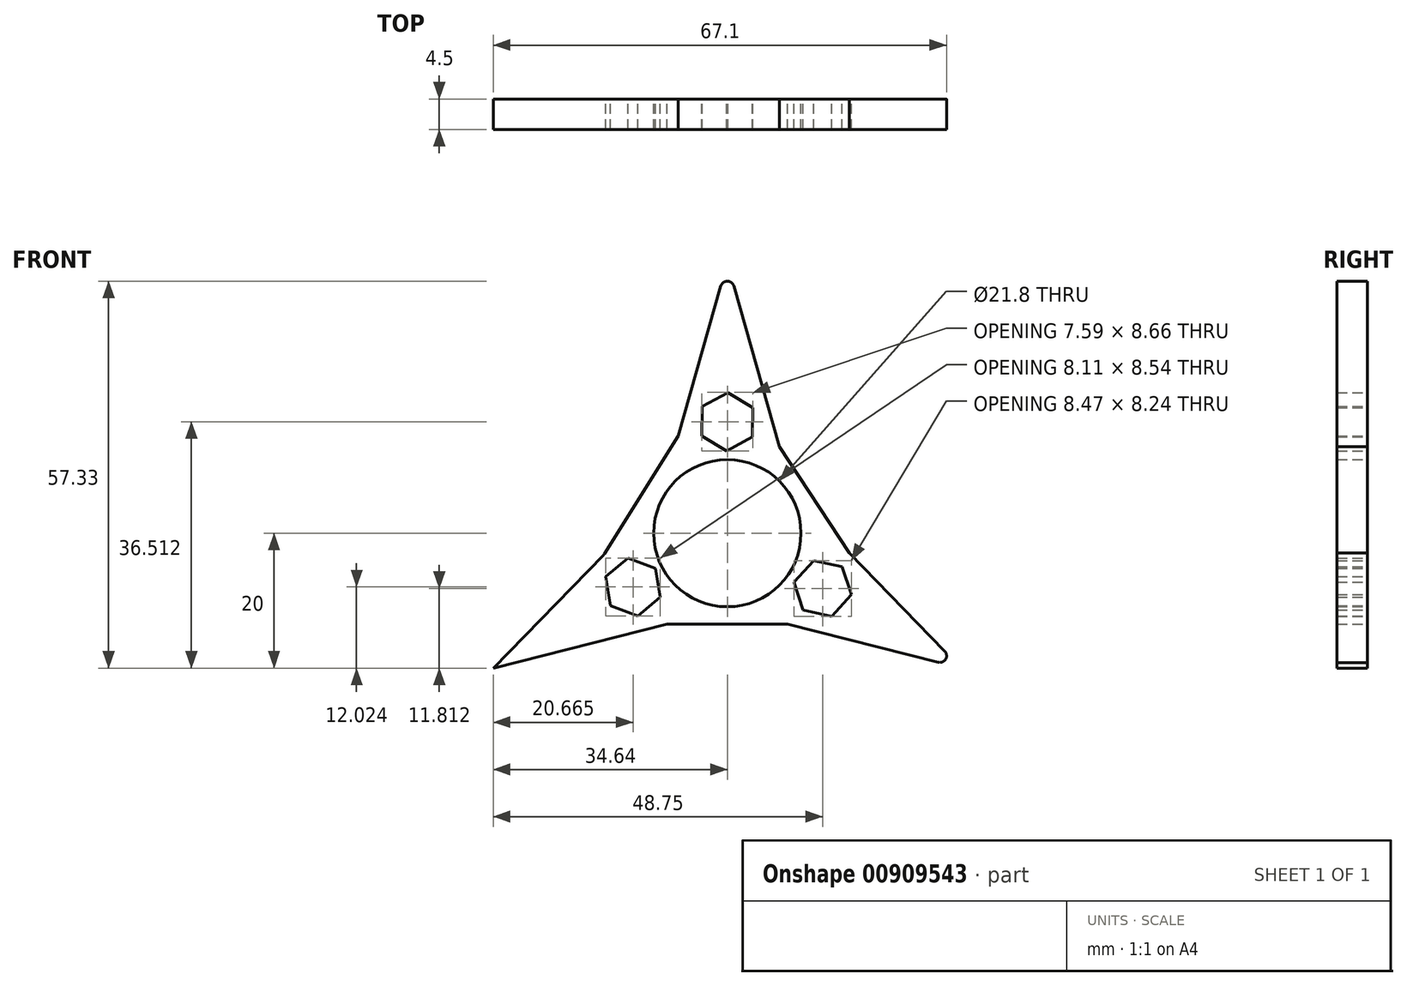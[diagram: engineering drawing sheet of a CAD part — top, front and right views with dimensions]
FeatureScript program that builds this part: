
annotation { "Feature Type Name" : "Feature", "Feature Type Description" : "" }
export const myFeature = defineFeature(function(context is Context, id is Id, definition is map)
    precondition{}
    {
        {
            var Q0;
            Q0=qCreatedBy(makeId("Front.planeOp"),FACE);
            var sketch = newSketch(context, id + "F0", { "sketchPlane" : qUnion([Q0])});
            skCircle(sketch, "E0", {"center": v(0, 0) * mm, "radius": 10.9 * mm});
            skLineSegment(sketch, "E1", {"start": v(0, 0) * mm, "end": v(0, 40) * mm});
            skLineSegment(sketch, "E2", {"start": v(0, 0) * mm, "end": v(34.64, -20) * mm});
            skPoint(sketch, "E3.MirrorCS.start.orphan", {"position": v(0, 40) * mm});
            skLineSegment(sketch, "E4", {"start": v(0, 40) * mm, "end": v(7.7, 12.82) * mm});
            skLineSegment(sketch, "E5", {"start": v(0, 0) * mm, "end": v(-34.64, -20) * mm});
            skPoint(sketch, "E6.MirrorP", {"position": v(-34.64, -20) * mm});
            skLineSegment(sketch, "E7.MirrorCS", {"start": v(-34.64, -20) * mm, "end": v(-18.27, -3.15) * mm});
            skLineSegment(sketch, "E8.MirrorCS", {"start": v(-34.64, -20) * mm, "end": v(-8.93, -13.5) * mm});
            skLineSegment(sketch, "E9.MirrorCS", {"start": v(0, 40) * mm, "end": v(-7.26, 14.37) * mm});
            skLineSegment(sketch, "E10.MirrorCS", {"start": v(34.64, -20) * mm, "end": v(18.08, -2.97) * mm});
            skLineSegment(sketch, "E11.MirrorCS", {"start": v(34.64, -20) * mm, "end": v(8.93, -13.5) * mm});
            skLineSegment(sketch, "E12", {"start": v(7.7, 12.82) * mm, "end": v(18.08, -2.97) * mm});
            skLineSegment(sketch, "E13", {"start": v(-7.26, 14.37) * mm, "end": v(-18.27, -3.15) * mm});
            skLineSegment(sketch, "E14", {"start": v(8.93, -13.5) * mm, "end": v(-8.93, -13.5) * mm});
            skPoint(sketch, "E15.orphan", {"position": v(15.2, 0) * mm});
            skPoint(sketch, "E16.end.orphan", {"position": v(-15.2, 0) * mm});
            skSolve(sketch);
        }
        {
            var Q0;
            Q0=qSketchRegion(id+"F0",true);
            extrude(context, id + "F1", {"entities" : qUnion([Q0]), "depth" : 4.5 * mm, "offsetDistance" : 25 * mm});
        }
        {
            var Q0;
            Q0=makeQuery(id+"F1.opExtrude","SWEPT_EDGE",EDGE,{"disambiguationData":[OSD([sQuery(id+"F0.wireOp",EDGE,"E1"),sQuery(id+"F0.wireOp",EDGE,"E4"),sQuery(id+"F0.wireOp",EDGE,"E9.MirrorCS")])]});
            var Q1;
            Q1=makeQuery(id+"F1.opExtrude","SWEPT_EDGE",EDGE,{"disambiguationData":[OSD([sQuery(id+"F0.wireOp",EDGE,"E2"),sQuery(id+"F0.wireOp",EDGE,"E10.MirrorCS"),sQuery(id+"F0.wireOp",EDGE,"E11.MirrorCS")])]});
            var Q2;
            Q2=makeQuery(id+"F1.opExtrude","SWEPT_EDGE",EDGE,{"disambiguationData":[OSD([sQuery(id+"F0.wireOp",EDGE,"E7.MirrorCS"),sQuery(id+"F0.wireOp",EDGE,"E5"),sQuery(id+"F0.wireOp",EDGE,"E8.MirrorCS")])]});
            fillet(context, id + "F2", {"entities" : qUnion([Q0, Q1, Q2]), "radius" : 1 * mm, "tangentPropagation" : true, "allowEdgeOverflow" : false});
        }
        {
            var Q0;
            Q0=makeQuery(id+"F1.opExtrude","CAP_FACE",FACE,{"disambiguationData":[OSD([sQuery(id+"F0.wireOp",EDGE,"E0"),sQuery(id+"F0.wireOp",EDGE,"E4"),sQuery(id+"F0.wireOp",EDGE,"E7.MirrorCS"),sQuery(id+"F0.wireOp",EDGE,"E9.MirrorCS"),sQuery(id+"F0.wireOp",EDGE,"E8.MirrorCS"),sQuery(id+"F0.wireOp",EDGE,"E10.MirrorCS"),sQuery(id+"F0.wireOp",EDGE,"E11.MirrorCS"),sQuery(id+"F0.wireOp",EDGE,"E16"),sQuery(id+"F0.wireOp",EDGE,"dIhDfe71-4vUS-nJFN-CgB5-YhKECHlm1RoW"),sQuery(id+"F0.wireOp",EDGE,"exgupVJA-VvQW-esT0-tabG-CJ82kmzNKVRX")])],"isStart":true});
            var sketch = newSketch(context, id + "F3", { "sketchPlane" : qUnion([Q0])});
            skCircle(sketch, "E17.cCircle", {"center": v(-14.11, -8.19) * mm, "radius": 3.75 * mm, "construction": true});
            skLineSegment(sketch, "E17.0", {"start": v(-9.88, -7.29) * mm, "end": v(-11.21, -11.4) * mm});
            skLineSegment(sketch, "E17.1", {"start": v(-11.21, -11.4) * mm, "end": v(-15.45, -12.3) * mm});
            skLineSegment(sketch, "E17.2", {"start": v(-15.45, -12.3) * mm, "end": v(-18.35, -9.1) * mm});
            skLineSegment(sketch, "E17.3", {"start": v(-18.35, -9.1) * mm, "end": v(-17, -4.97) * mm});
            skLineSegment(sketch, "E17.4", {"start": v(-17, -4.97) * mm, "end": v(-12.77, -4.07) * mm});
            skLineSegment(sketch, "E17.5", {"start": v(-12.77, -4.07) * mm, "end": v(-9.88, -7.29) * mm});
            skPoint(sketch, "E17.0.midPoint", {"position": v(-10.54, -9.34) * mm});
            skCircle(sketch, "E18.cCircle", {"center": v(13.97, -7.98) * mm, "radius": 3.75 * mm, "construction": true});
            skLineSegment(sketch, "E18.0", {"start": v(18.03, -6.45) * mm, "end": v(17.32, -10.72) * mm});
            skLineSegment(sketch, "E18.1", {"start": v(17.32, -10.72) * mm, "end": v(13.27, -12.25) * mm});
            skLineSegment(sketch, "E18.2", {"start": v(13.27, -12.25) * mm, "end": v(9.92, -9.5) * mm});
            skLineSegment(sketch, "E18.3", {"start": v(9.92, -9.5) * mm, "end": v(10.63, -5.23) * mm});
            skLineSegment(sketch, "E18.4", {"start": v(10.63, -5.23) * mm, "end": v(14.68, -3.7) * mm});
            skLineSegment(sketch, "E18.5", {"start": v(14.68, -3.7) * mm, "end": v(18.03, -6.45) * mm});
            skPoint(sketch, "E18.0.midPoint", {"position": v(17.67, -8.59) * mm});
            skCircle(sketch, "E19.cCircle", {"center": v(0, 16.51) * mm, "radius": 3.75 * mm, "construction": true});
            skLineSegment(sketch, "E19.0", {"start": v(3.8, 14.43) * mm, "end": v(0.1, 12.18) * mm});
            skLineSegment(sketch, "E19.1", {"start": v(0.1, 12.18) * mm, "end": v(-3.7, 14.27) * mm});
            skLineSegment(sketch, "E19.2", {"start": v(-3.7, 14.27) * mm, "end": v(-3.8, 18.6) * mm});
            skLineSegment(sketch, "E19.3", {"start": v(-3.8, 18.6) * mm, "end": v(-0.1, 20.84) * mm});
            skLineSegment(sketch, "E19.4", {"start": v(-0.1, 20.84) * mm, "end": v(3.7, 18.76) * mm});
            skLineSegment(sketch, "E19.5", {"start": v(3.7, 18.76) * mm, "end": v(3.8, 14.43) * mm});
            skPoint(sketch, "E19.0.midPoint", {"position": v(1.94, 13.3) * mm});
            skSolve(sketch);
        }
        {
            var Q0;
            Q0=qSketchRegion(id+"F3",true);
            extrude(context, id + "F4", {"entities" : qUnion([Q0]), "operationType" : NewBodyOperationType.REMOVE, "oppositeDirection" : true, "depth" : 25 * mm, "offsetDistance" : 25 * mm});
        }
    });
